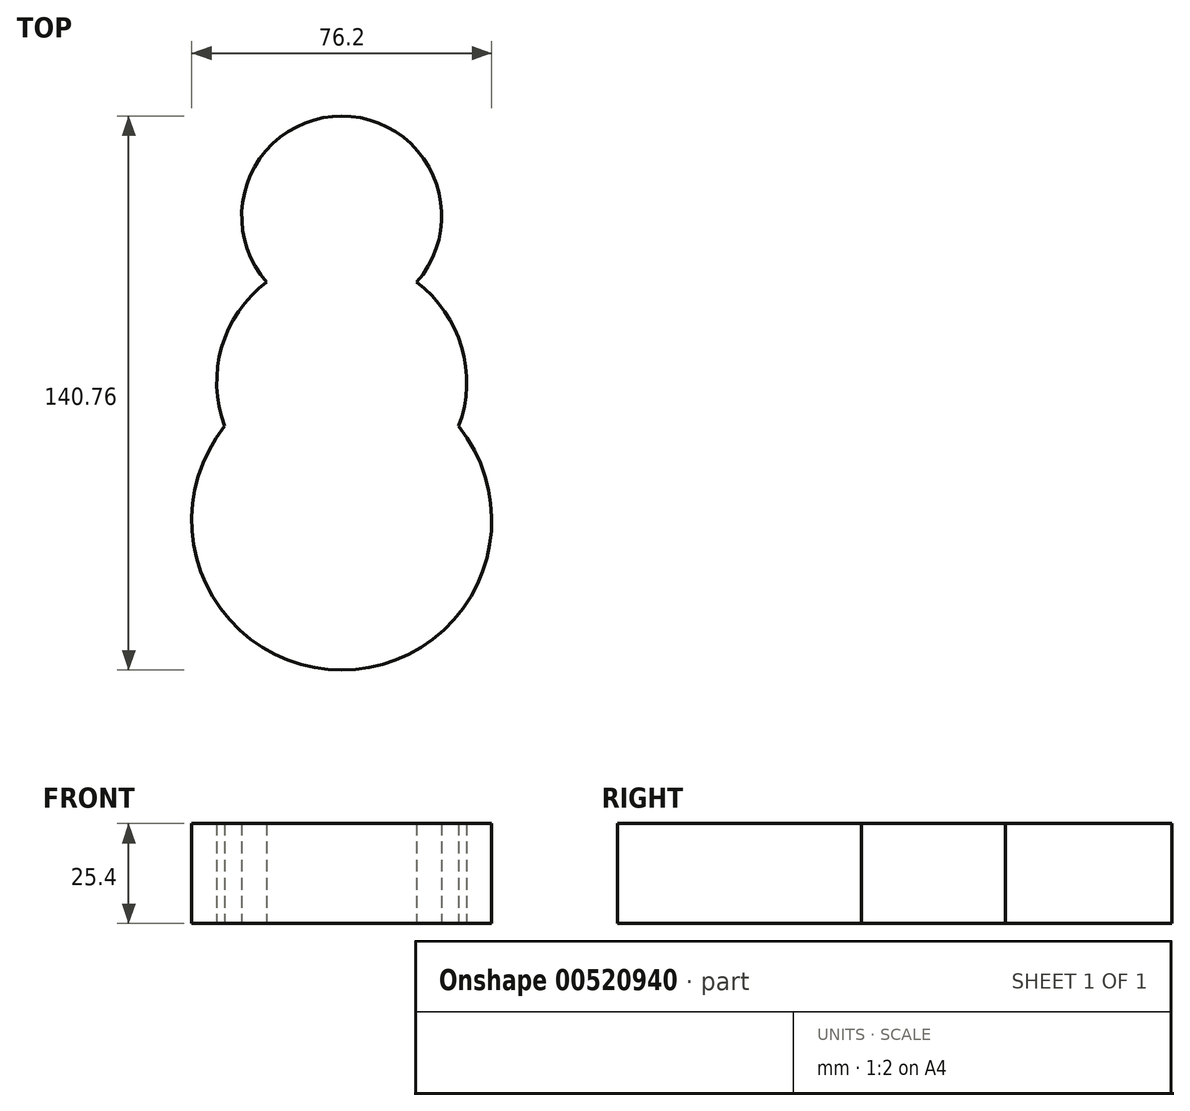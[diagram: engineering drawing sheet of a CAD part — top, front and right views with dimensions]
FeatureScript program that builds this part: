
annotation { "Feature Type Name" : "Feature", "Feature Type Description" : "" }
export const myFeature = defineFeature(function(context is Context, id is Id, definition is map)
    precondition{}
    {
        {
            var Q0;
            Q0=qCreatedBy(makeId("Top.planeOp"),FACE);
            var sketch = newSketch(context, id + "F0", { "sketchPlane" : qUnion([Q0])});
            skCircle(sketch, "E0", {"center": v(0, 0) * mm, "radius": 31.75 * mm});
            skCircle(sketch, "E1", {"center": v(0, 42.2) * mm, "radius": 25.4 * mm});
            skCircle(sketch, "E2", {"center": v(0, -35.06) * mm, "radius": 38.1 * mm});
            skSolve(sketch);
        }
        {
            var Q0;
            {var subQ0=sQuery(id+"F0.wireOp",EDGE,"E1");var subQ1=sQuery(id+"F0.wireOp",EDGE,"E0");var subQ2=makeQuery(id+"F0.imprint","INTERSECT",VERTEX,{"disambiguationData":[OD(0.0)],"derivedFrom":[subQ1,subQ0]});Q0=makeQuery(id+"F0.imprint","IMPRINT",FACE,{"disambiguationData":[TD([[makeQuery(id+"F0.imprint","IMPRINT",EDGE,{"disambiguationData":[TD([[subQ2,1.0]])],"derivedFrom":subQ1}),-1.0]])]});}
            var Q1;
            {var subQ0=sQuery(id+"F0.wireOp",EDGE,"E1");var subQ1=sQuery(id+"F0.wireOp",EDGE,"E0");var subQ2=makeQuery(id+"F0.imprint","INTERSECT",VERTEX,{"disambiguationData":[OD(0.0)],"derivedFrom":[subQ1,subQ0]});Q1=makeQuery(id+"F0.imprint","IMPRINT",FACE,{"disambiguationData":[TD([[makeQuery(id+"F0.imprint","IMPRINT",EDGE,{"disambiguationData":[TD([[subQ2,1.0]])],"derivedFrom":subQ1}),1.0]])]});}
            var Q2;
            {var subQ0=sQuery(id+"F0.wireOp",EDGE,"E1");var subQ1=sQuery(id+"F0.wireOp",EDGE,"E0");var subQ2=makeQuery(id+"F0.imprint","INTERSECT",VERTEX,{"disambiguationData":[OD(0.0)],"derivedFrom":[subQ1,subQ0]});Q2=makeQuery(id+"F0.imprint","IMPRINT",FACE,{"disambiguationData":[TD([[makeQuery(id+"F0.imprint","IMPRINT",EDGE,{"disambiguationData":[TD([[subQ2,-1.0]])],"derivedFrom":subQ1}),1.0]])]});}
            var Q3;
            {var subQ0=sQuery(id+"F0.wireOp",EDGE,"E2");var subQ1=sQuery(id+"F0.wireOp",EDGE,"E0");var subQ2=makeQuery(id+"F0.imprint","INTERSECT",VERTEX,{"disambiguationData":[OD(0.0)],"derivedFrom":[subQ1,subQ0]});Q3=makeQuery(id+"F0.imprint","IMPRINT",FACE,{"disambiguationData":[TD([[makeQuery(id+"F0.imprint","IMPRINT",EDGE,{"disambiguationData":[TD([[subQ2,-1.0]])],"derivedFrom":subQ1}),1.0]])]});}
            var Q4;
            {var subQ0=sQuery(id+"F0.wireOp",EDGE,"E2");var subQ1=sQuery(id+"F0.wireOp",EDGE,"E0");var subQ2=makeQuery(id+"F0.imprint","INTERSECT",VERTEX,{"disambiguationData":[OD(0.0)],"derivedFrom":[subQ1,subQ0]});Q4=makeQuery(id+"F0.imprint","IMPRINT",FACE,{"disambiguationData":[TD([[makeQuery(id+"F0.imprint","IMPRINT",EDGE,{"disambiguationData":[TD([[subQ2,-1.0]])],"derivedFrom":subQ1}),-1.0]])]});}
            extrude(context, id + "F1", {"entities" : qUnion([Q0, Q1, Q2, Q3, Q4]), "depth" : 25.4 * mm, "offsetDistance" : 25.4 * mm});
        }
    });
